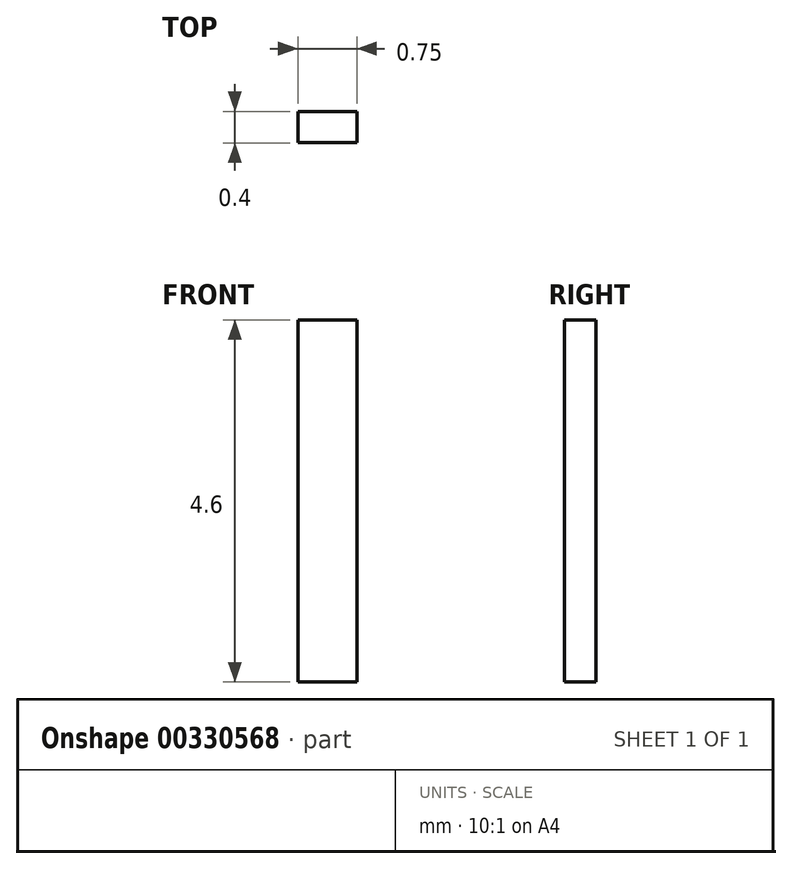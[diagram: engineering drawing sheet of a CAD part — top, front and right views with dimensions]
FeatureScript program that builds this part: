
annotation { "Feature Type Name" : "Feature", "Feature Type Description" : "" }
export const myFeature = defineFeature(function(context is Context, id is Id, definition is map)
    precondition{}
    {
        {
            var Q0;
            Q0=qCreatedBy(makeId("Top.planeOp"),FACE);
            var sketch = newSketch(context, id + "F0", { "sketchPlane" : qUnion([Q0])});
            skLineSegment(sketch, "E0.bottom", {"start": v(-22.87, 14.16) * mm, "end": v(-22.12, 14.16) * mm});
            skLineSegment(sketch, "E0.top", {"start": v(-22.87, 13.76) * mm, "end": v(-22.12, 13.76) * mm});
            skLineSegment(sketch, "E0.left", {"start": v(-22.87, 14.16) * mm, "end": v(-22.87, 13.76) * mm});
            skLineSegment(sketch, "E0.right", {"start": v(-22.12, 14.16) * mm, "end": v(-22.12, 13.76) * mm});
            skSolve(sketch);
        }
        {
            var Q0;
            Q0=makeQuery(id+"F0.imprint","IMPRINT",FACE,{"disambiguationData":[TD([[makeQuery(id+"F0.imprint","IMPRINT",EDGE,{"derivedFrom":sQuery(id+"F0.wireOp",EDGE,"E0.bottom")}),-1.0]])]});
            extrude(context, id + "F1", {"entities" : qUnion([Q0]), "depth" : 4.6 * mm});
        }
    });
